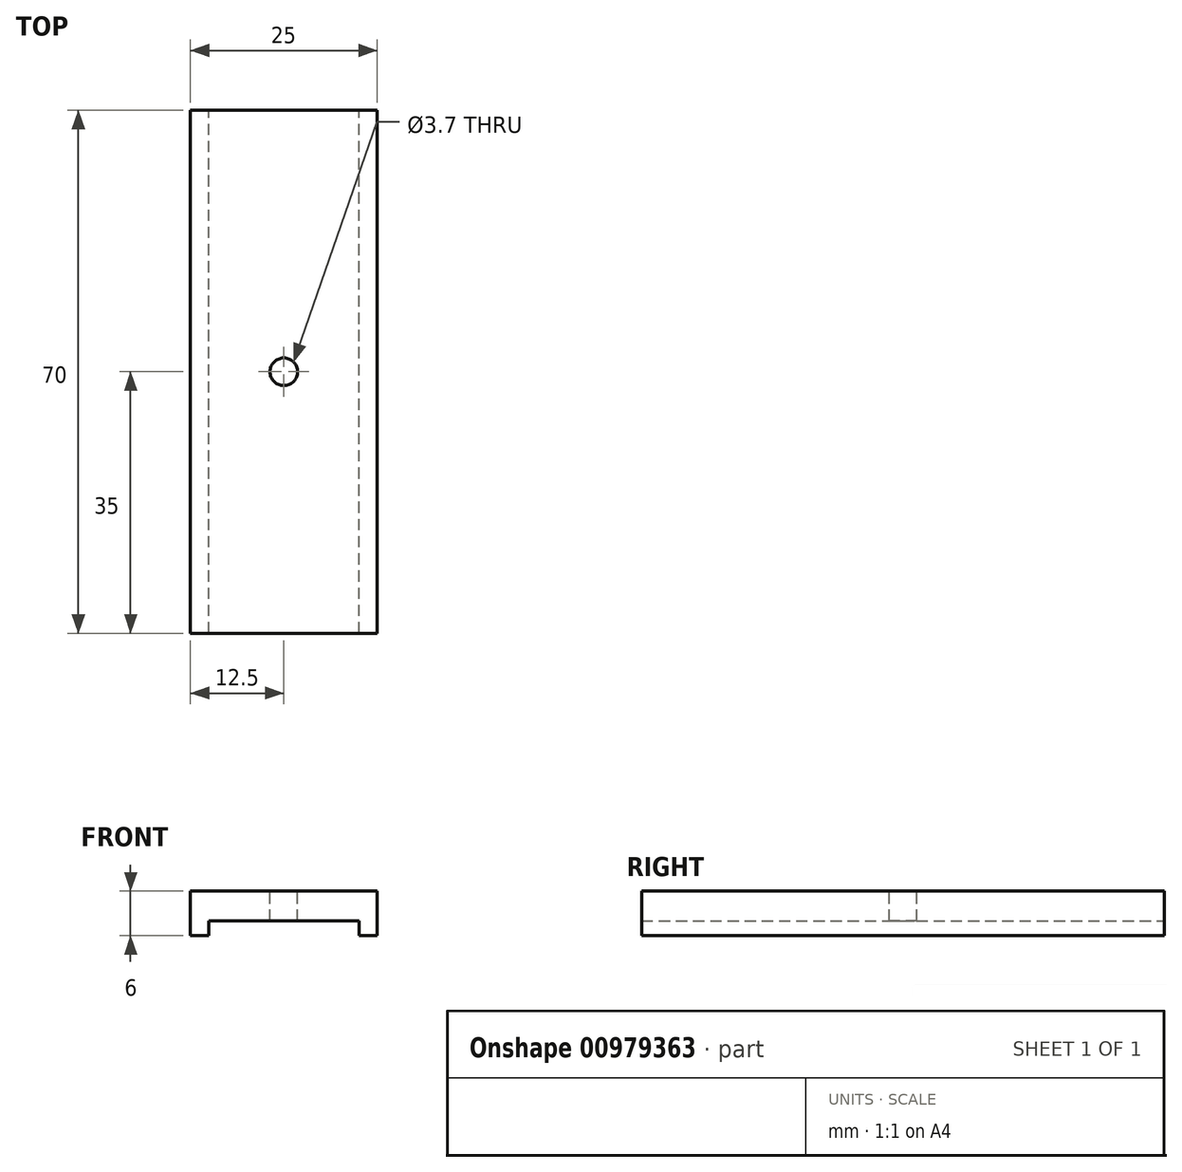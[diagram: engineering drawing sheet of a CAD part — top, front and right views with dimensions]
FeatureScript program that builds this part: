
annotation { "Feature Type Name" : "Feature", "Feature Type Description" : "" }
export const myFeature = defineFeature(function(context is Context, id is Id, definition is map)
    precondition{}
    {
        {
            var Q0;
            Q0=qCreatedBy(makeId("Front.planeOp"),FACE);
            var sketch = newSketch(context, id + "F0", { "sketchPlane" : qUnion([Q0])});
            skLineSegment(sketch, "E0.bottom", {"start": v(-10.06, 10) * mm, "end": v(10.06, 10) * mm});
            skLineSegment(sketch, "E0.top", {"start": v(-10.06, -10) * mm, "end": v(10.06, -10) * mm});
            skLineSegment(sketch, "E0.left", {"start": v(-10.06, 10) * mm, "end": v(-10.06, -10) * mm});
            skLineSegment(sketch, "E0.right", {"start": v(10.06, 10) * mm, "end": v(10.06, -10) * mm});
            skLineSegment(sketch, "E1.bottom", {"start": v(-12.5, 14) * mm, "end": v(12.5, 14) * mm});
            skLineSegment(sketch, "E1.top", {"start": v(-12.5, 8) * mm, "end": v(12.5, 8) * mm});
            skLineSegment(sketch, "E1.left", {"start": v(-12.5, 14) * mm, "end": v(-12.5, 8) * mm});
            skLineSegment(sketch, "E1.right", {"start": v(12.5, 14) * mm, "end": v(12.5, 8) * mm});
            skSolve(sketch);
        }
        {
            var Q0;
            {var subQ1=sQuery(id+"F0.wireOp",EDGE,"E0.bottom");Q0=makeQuery(id+"F0.imprint","IMPRINT",FACE,{"disambiguationData":[TD([[makeQuery(id+"F0.imprint","IMPRINT",EDGE,{"derivedFrom":subQ1}),1.0]])]});}
            extrude(context, id + "F1", {"entities" : qUnion([Q0]), "endBound" : BoundingType.SYMMETRIC, "depth" : 70 * mm, "offsetDistance" : 25 * mm});
        }
        {
            var Q0;
            Q0=makeQuery(id+"F1.opExtrude","SWEPT_FACE",FACE,{"disambiguationData":[OSD([sQuery(id+"F0.wireOp",EDGE,"E1.bottom")])]});
            var sketch = newSketch(context, id + "F2", { "sketchPlane" : qUnion([Q0])});
            skCircle(sketch, "E2", {"center": v(0, 0) * mm, "radius": 1.85 * mm});
            skSolve(sketch);
        }
        {
            var Q0;
            Q0=makeQuery(id+"F2.imprint","IMPRINT",FACE,{"disambiguationData":[TD([[makeQuery(id+"F2.imprint","IMPRINT",EDGE,{"derivedFrom":sQuery(id+"F2.wireOp",EDGE,"kE5JHCc4-si4Y-zEiX-ccqG-dXARs12rkecv")}),1.0]])]});
            var Q1;
            Q1=makeQuery(id+"F2.imprint","IMPRINT",FACE,{"disambiguationData":[TD([[makeQuery(id+"F2.imprint","IMPRINT",EDGE,{"derivedFrom":sQuery(id+"F2.wireOp",EDGE,"edb439af-2e81-4af6-b581-ef0ca5e0f7820.MirrorC")}),-1.0]])]});
            var Q2;
            Q2=makeQuery(id+"F2.imprint","IMPRINT",FACE,{"disambiguationData":[TD([[makeQuery(id+"F2.imprint","IMPRINT",EDGE,{"derivedFrom":sQuery(id+"F2.wireOp",EDGE,"8fDsB1Qw-g0c6-97bM-2T1U-MTEiixhqgEMZ")}),1.0]])]});
            var Q3;
            Q3=makeQuery(id+"F2.imprint","IMPRINT",FACE,{"disambiguationData":[TD([[makeQuery(id+"F2.imprint","IMPRINT",EDGE,{"derivedFrom":sQuery(id+"F2.wireOp",EDGE,"5f5269ca-2103-411c-9bbf-2a1605efe12b0.MirrorC")}),-1.0]])]});
            var Q4;
            {var subQ0=sQuery(id+"F2.wireOp",EDGE,"eJXFnHqn-P3qE-hyPI-KuuO-yAX2emgJhhXQ.right");var subQ1=sQuery(id+"F2.wireOp",EDGE,"eJXFnHqn-P3qE-hyPI-KuuO-yAX2emgJhhXQ.bottom");var subQ2=makeQuery(id+"F2.imprint","INTERSECT",VERTEX,{"derivedFrom":[subQ1,subQ0]});Q4=makeQuery(id+"F2.imprint","IMPRINT",FACE,{"disambiguationData":[TD([[makeQuery(id+"F2.imprint","IMPRINT",EDGE,{"disambiguationData":[TD([[subQ2,1.0]])],"derivedFrom":subQ1}),-1.0]])]});}
            var Q5;
            {var subQ0=sQuery(id+"F2.wireOp",EDGE,"eJXFnHqn-P3qE-hyPI-KuuO-yAX2emgJhhXQ.right");var subQ1=sQuery(id+"F2.wireOp",EDGE,"eJXFnHqn-P3qE-hyPI-KuuO-yAX2emgJhhXQ.top");var subQ2=makeQuery(id+"F2.imprint","INTERSECT",VERTEX,{"derivedFrom":[subQ1,subQ0]});Q5=makeQuery(id+"F2.imprint","IMPRINT",FACE,{"disambiguationData":[TD([[makeQuery(id+"F2.imprint","IMPRINT",EDGE,{"disambiguationData":[TD([[subQ2,1.0]])],"derivedFrom":subQ1}),1.0]])]});}
            var Q6;
            {var subQ5=sQuery(id+"F2.wireOp",EDGE,"eJXFnHqn-P3qE-hyPI-KuuO-yAX2emgJhhXQ.left");Q6=makeQuery(id+"F2.imprint","IMPRINT",FACE,{"disambiguationData":[TD([[makeQuery(id+"F2.imprint","IMPRINT",EDGE,{"derivedFrom":subQ5}),1.0]])]});}
            var Q7;
            Q7=makeQuery(id+"F2.imprint","IMPRINT",FACE,{"disambiguationData":[TD([[makeQuery(id+"F2.imprint","IMPRINT",EDGE,{"derivedFrom":sQuery(id+"F2.wireOp",EDGE,"E2")}),1.0]])]});
            var Q8;
            Q8=makeQuery(id+"F2.imprint","IMPRINT",FACE,{"disambiguationData":[TD([[makeQuery(id+"F2.imprint","IMPRINT",EDGE,{"derivedFrom":sQuery(id+"F2.wireOp",EDGE,"cc838e83-06ba-4640-93d8-9c8a30ed6c410.MirrorC")}),-1.0]])]});
            extrude(context, id + "F3", {"entities" : qUnion([Q0, Q1, Q2, Q3, Q4, Q5, Q6, Q7, Q8]), "operationType" : NewBodyOperationType.REMOVE, "endBound" : BoundingType.THROUGH_ALL, "oppositeDirection" : true, "depth" : 25 * mm, "offsetDistance" : 25 * mm});
        }
    });
